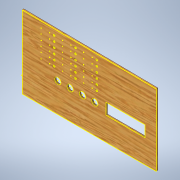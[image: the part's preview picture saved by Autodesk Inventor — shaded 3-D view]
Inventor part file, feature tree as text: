
AUTODESK INVENTOR PART (.ipt)
format: ipt  version: 2021 (Build 250183000, 183)  size: 274,432 bytes
history: native  units: mm
features: sketch x5, extrude x4, pattern_linear x2, thicken_offset x1, projected_geometry x1
ambient origin geometry x8: Origin, YZ Plane, XZ Plane, XY Plane, X Axis, Y Axis, Z Axis, Center Point
bodies: Solid1 (feature_tree)
feature tree (13):
  extrude  "Extrusion1"  Depth=630.0mm
  extrude  "Extrusion2"  Depth=8.0mm
  extrude  "Extrusion3"  Depth=183.0mm
  extrude  "Extrusion5"  Depth=53.0mm
  pattern_linear  "Rectangular Pattern3"  Spacing1=8.0mm  [1 undecoded]
  pattern_linear  "Rectangular Pattern4"  Spacing1=0.0mm  [1 undecoded]
  thicken_offset  "Thicken1"
  sketch  "Sketch6"  dims[d8=35.333333mm d9=8.0mm d10=0.0mm d11=8.0mm d13=25.0mm d14=8.0mm d15=0.0mm d26=29.0mm d27=53.0mm d28=8.0mm d29=0.0mm d30=40.0mm d32=58.0mm d36=150.0mm d37=30.0mm d39=100.0mm d40=60.0mm d42=25.0mm d43=75.0mm d44=75.0mm d45=20.0mm d46=1.0mm d47=40.0mm]
  sketch  "Sketch1"  dims[d0=630.0mm d1=260.0mm]
  sketch  "Sketch2"  dims[d2=267.0mm d3=8.0mm]
  sketch  "Sketch3"  dims[d4=0.0mm d5=183.0mm]
  sketch  "Sketch5"  dims[d6=53.0mm d7=53.0mm]
  projected_geometry  "Projected Loop1"
note: 2 required parameter values undecoded (feature->parameter linkage not recoverable at this tier; creation-order binding heuristic only, values carry confidence <= 0.55)
